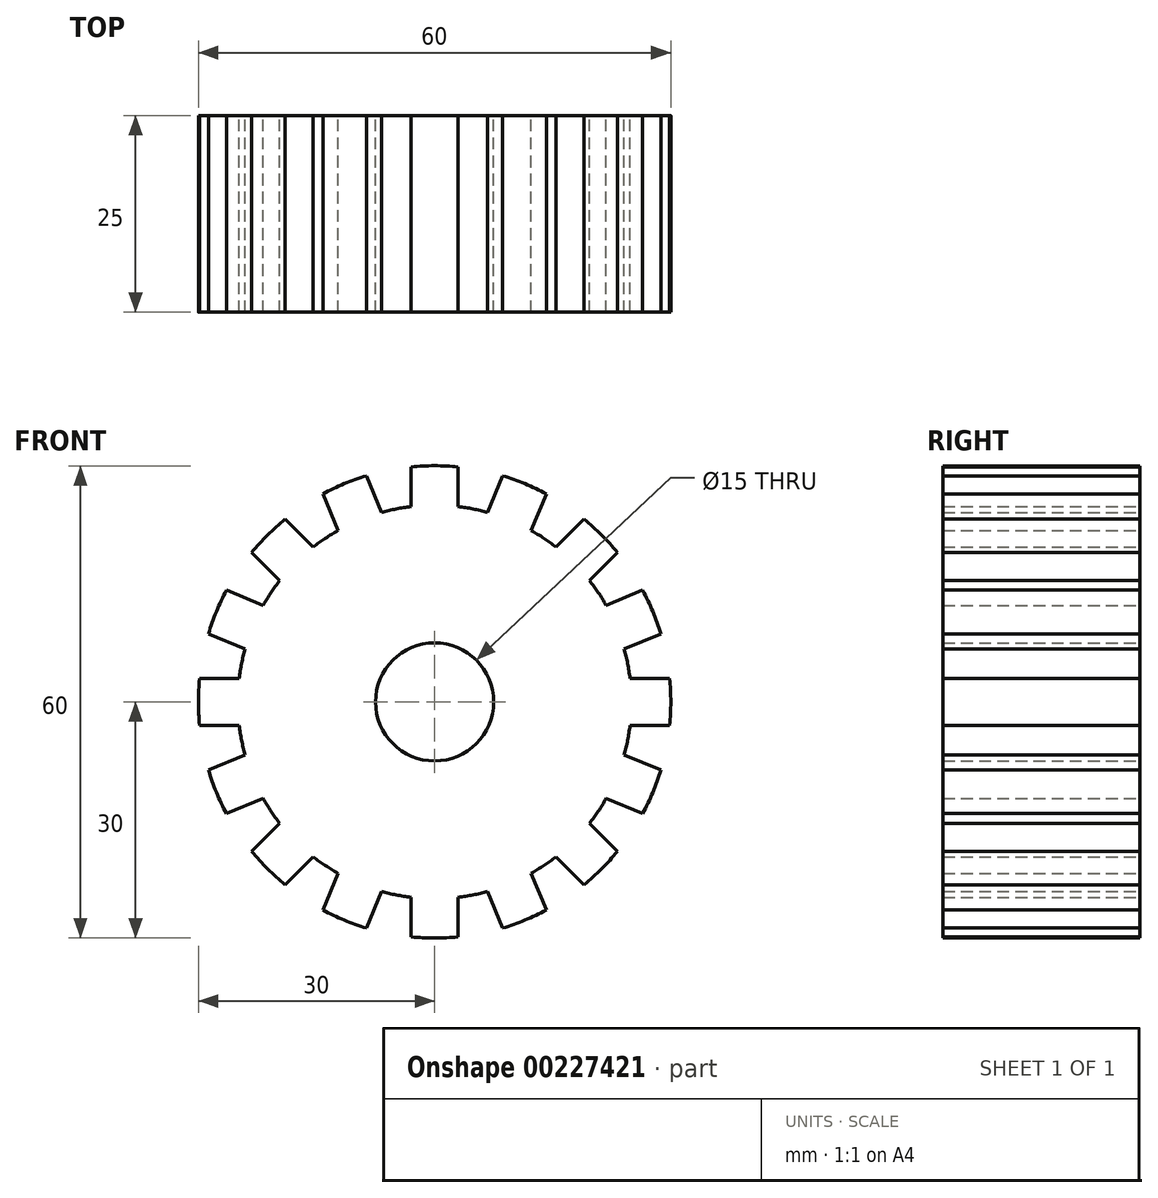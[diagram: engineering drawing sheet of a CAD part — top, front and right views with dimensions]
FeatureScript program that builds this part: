
annotation { "Feature Type Name" : "Feature", "Feature Type Description" : "" }
export const myFeature = defineFeature(function(context is Context, id is Id, definition is map)
    precondition{}
    {
        {
            var Q0;
            Q0=qCreatedBy(makeId("Front.planeOp"),FACE);
            var sketch = newSketch(context, id + "F0", { "sketchPlane" : qUnion([Q0])});
            skCircle(sketch, "E0", {"center": v(0, 0) * mm, "radius": 7.5 * mm});
            skCircle(sketch, "E1", {"center": v(0, 0) * mm, "radius": 15 * mm, "construction": true});
            skArc(sketch, "E2", {"start": v(3, 29.85) * mm, "mid": v(0, 30) * mm, "end": v(-3, 29.85) * mm});
            skArc(sketch, "E3", {"start": v(-3, 24.82) * mm, "mid": v(0, -25) * mm, "end": v(3, 24.82) * mm});
            skLineSegment(sketch, "E4", {"start": v(-3, 29.85) * mm, "end": v(-3, 24.82) * mm});
            skLineSegment(sketch, "E5", {"start": v(3, 29.85) * mm, "end": v(3, 24.82) * mm});
            skLineSegment(sketch, "E6.1.0", {"start": v(-14.2, 26.43) * mm, "end": v(-12.27, 21.78) * mm});
            skArc(sketch, "E6.1.1", {"start": v(-8.65, 28.73) * mm, "mid": v(-11.48, 27.72) * mm, "end": v(-14.2, 26.43) * mm});
            skLineSegment(sketch, "E6.1.2", {"start": v(-8.65, 28.73) * mm, "end": v(-6.73, 24.08) * mm});
            skLineSegment(sketch, "E6.2.0", {"start": v(-23.23, 18.99) * mm, "end": v(-19.67, 15.43) * mm});
            skArc(sketch, "E6.2.1", {"start": v(-18.99, 23.23) * mm, "mid": v(-21.21, 21.21) * mm, "end": v(-23.23, 18.99) * mm});
            skLineSegment(sketch, "E6.2.2", {"start": v(-18.99, 23.23) * mm, "end": v(-15.43, 19.67) * mm});
            skLineSegment(sketch, "E6.3.0", {"start": v(-28.73, 8.65) * mm, "end": v(-24.08, 6.73) * mm});
            skArc(sketch, "E6.3.1", {"start": v(-26.43, 14.2) * mm, "mid": v(-27.72, 11.48) * mm, "end": v(-28.73, 8.65) * mm});
            skLineSegment(sketch, "E6.3.2", {"start": v(-26.43, 14.2) * mm, "end": v(-21.78, 12.27) * mm});
            skLineSegment(sketch, "E6.4.0", {"start": v(-29.85, -3) * mm, "end": v(-24.82, -3) * mm});
            skArc(sketch, "E6.4.1", {"start": v(-29.85, 3) * mm, "mid": v(-30, 0) * mm, "end": v(-29.85, -3) * mm});
            skLineSegment(sketch, "E6.4.2", {"start": v(-29.85, 3) * mm, "end": v(-24.82, 3) * mm});
            skLineSegment(sketch, "E6.5.0", {"start": v(-26.43, -14.2) * mm, "end": v(-21.78, -12.27) * mm});
            skArc(sketch, "E6.5.1", {"start": v(-28.73, -8.65) * mm, "mid": v(-27.72, -11.48) * mm, "end": v(-26.43, -14.2) * mm});
            skLineSegment(sketch, "E6.5.2", {"start": v(-28.73, -8.65) * mm, "end": v(-24.08, -6.73) * mm});
            skLineSegment(sketch, "E6.6.0", {"start": v(-18.99, -23.23) * mm, "end": v(-15.43, -19.67) * mm});
            skArc(sketch, "E6.6.1", {"start": v(-23.23, -18.99) * mm, "mid": v(-21.21, -21.21) * mm, "end": v(-18.99, -23.23) * mm});
            skLineSegment(sketch, "E6.6.2", {"start": v(-23.23, -18.99) * mm, "end": v(-19.67, -15.43) * mm});
            skLineSegment(sketch, "E6.7.0", {"start": v(-8.65, -28.73) * mm, "end": v(-6.73, -24.08) * mm});
            skArc(sketch, "E6.7.1", {"start": v(-14.2, -26.43) * mm, "mid": v(-11.48, -27.72) * mm, "end": v(-8.65, -28.73) * mm});
            skLineSegment(sketch, "E6.7.2", {"start": v(-14.2, -26.43) * mm, "end": v(-12.27, -21.78) * mm});
            skLineSegment(sketch, "E6.8.0", {"start": v(3, -29.85) * mm, "end": v(3, -24.82) * mm});
            skArc(sketch, "E6.8.1", {"start": v(-3, -29.85) * mm, "mid": v(0, -30) * mm, "end": v(3, -29.85) * mm});
            skLineSegment(sketch, "E6.8.2", {"start": v(-3, -29.85) * mm, "end": v(-3, -24.82) * mm});
            skLineSegment(sketch, "E6.9.0", {"start": v(14.2, -26.43) * mm, "end": v(12.27, -21.78) * mm});
            skArc(sketch, "E6.9.1", {"start": v(8.65, -28.73) * mm, "mid": v(11.48, -27.72) * mm, "end": v(14.2, -26.43) * mm});
            skLineSegment(sketch, "E6.9.2", {"start": v(8.65, -28.73) * mm, "end": v(6.73, -24.08) * mm});
            skLineSegment(sketch, "E6.10.0", {"start": v(23.23, -18.99) * mm, "end": v(19.67, -15.43) * mm});
            skArc(sketch, "E6.10.1", {"start": v(18.99, -23.23) * mm, "mid": v(21.21, -21.21) * mm, "end": v(23.23, -18.99) * mm});
            skLineSegment(sketch, "E6.10.2", {"start": v(18.99, -23.23) * mm, "end": v(15.43, -19.67) * mm});
            skLineSegment(sketch, "E6.11.0", {"start": v(28.73, -8.65) * mm, "end": v(24.08, -6.73) * mm});
            skArc(sketch, "E6.11.1", {"start": v(26.43, -14.2) * mm, "mid": v(27.72, -11.48) * mm, "end": v(28.73, -8.65) * mm});
            skLineSegment(sketch, "E6.11.2", {"start": v(26.43, -14.2) * mm, "end": v(21.78, -12.27) * mm});
            skLineSegment(sketch, "E6.12.0", {"start": v(29.85, 3) * mm, "end": v(24.82, 3) * mm});
            skArc(sketch, "E6.12.1", {"start": v(29.85, -3) * mm, "mid": v(30, 0) * mm, "end": v(29.85, 3) * mm});
            skLineSegment(sketch, "E6.12.2", {"start": v(29.85, -3) * mm, "end": v(24.82, -3) * mm});
            skLineSegment(sketch, "E6.13.0", {"start": v(26.43, 14.2) * mm, "end": v(21.78, 12.27) * mm});
            skArc(sketch, "E6.13.1", {"start": v(28.73, 8.65) * mm, "mid": v(27.72, 11.48) * mm, "end": v(26.43, 14.2) * mm});
            skLineSegment(sketch, "E6.13.2", {"start": v(28.73, 8.65) * mm, "end": v(24.08, 6.73) * mm});
            skLineSegment(sketch, "E6.14.0", {"start": v(18.99, 23.23) * mm, "end": v(15.43, 19.67) * mm});
            skArc(sketch, "E6.14.1", {"start": v(23.23, 18.99) * mm, "mid": v(21.21, 21.21) * mm, "end": v(18.99, 23.23) * mm});
            skLineSegment(sketch, "E6.14.2", {"start": v(23.23, 18.99) * mm, "end": v(19.67, 15.43) * mm});
            skLineSegment(sketch, "E6.15.0", {"start": v(8.65, 28.73) * mm, "end": v(6.73, 24.08) * mm});
            skArc(sketch, "E6.15.1", {"start": v(14.2, 26.43) * mm, "mid": v(11.48, 27.72) * mm, "end": v(8.65, 28.73) * mm});
            skLineSegment(sketch, "E6.15.2", {"start": v(14.2, 26.43) * mm, "end": v(12.27, 21.78) * mm});
            skPoint(sketch, "E7", {"position": v(0, 30) * mm});
            skSolve(sketch);
        }
        {
            var Q0;
            Q0 = qSketchRegion(id + "F0", true);
            extrude(context, id + "F1", {"entities" : qUnion([Q0]), "depth" : 25 * mm});
        }
    });
